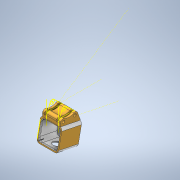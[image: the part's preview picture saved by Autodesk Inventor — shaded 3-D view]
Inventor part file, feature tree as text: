
AUTODESK INVENTOR PART (.ipt)
format: ipt  version: 2020 (Build 240168000, 168)  size: 274,944 bytes
history: native  units: mm
features: other x4, sketch x4
ambient origin geometry x8: Origin, YZ Plane, XZ Plane, XY Plane, X Axis, Y Axis, Z Axis, Center Point
bodies: Solid1 (feature_tree)
feature tree (8):
  other  "V2 modular session micro cam adj mount 45 deg.iam"
  other  "V2 session mount 45deg block.ipt:1"
  other  "Kauri modular camera mount HDzero micro v1.ipt:1"
  other  "Kauri modular camera mount HDzero micro v1.ipt:2"
  sketch  "Sketch6"
  sketch  "Sketch7"
  sketch  "Sketch2"
  sketch  "Sketch2_1"  dims[d0=10.0mm]
